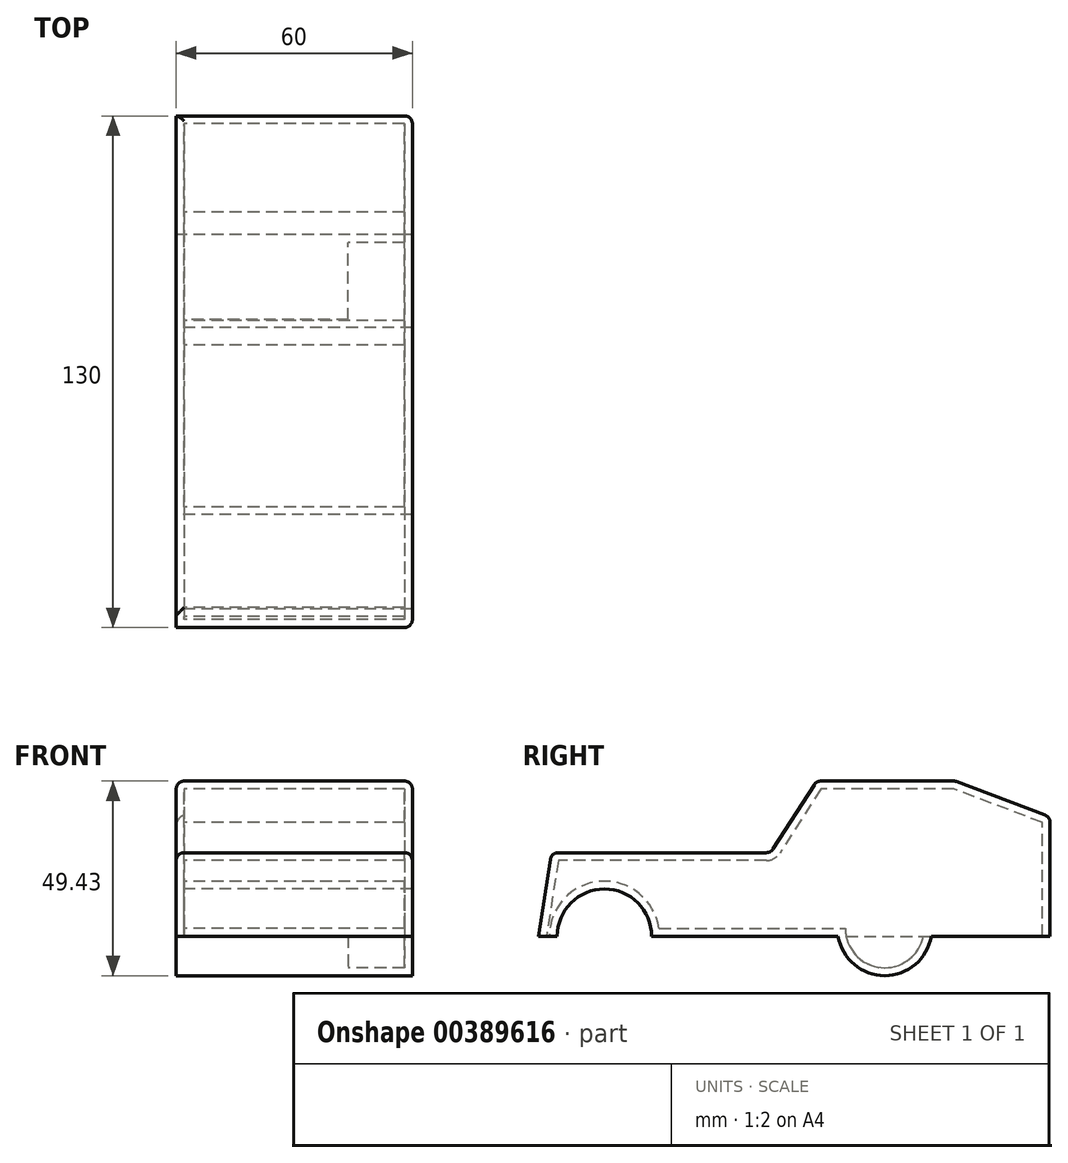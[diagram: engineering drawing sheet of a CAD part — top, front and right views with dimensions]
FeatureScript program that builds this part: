
annotation { "Feature Type Name" : "Feature", "Feature Type Description" : "" }
export const myFeature = defineFeature(function(context is Context, id is Id, definition is map)
    precondition{}
    {
        {
            var Q0;
            Q0=qCreatedBy(makeId("Right.planeOp"),FACE);
            var sketch = newSketch(context, id + "F0", { "sketchPlane" : qUnion([Q0])});
            skLineSegment(sketch, "E0", {"start": v(-47.15, 0) * mm, "end": v(82.85, 0) * mm});
            skLineSegment(sketch, "E1", {"start": v(82.85, 0) * mm, "end": v(82.85, 30.3) * mm});
            skLineSegment(sketch, "E2", {"start": v(82.85, 30.3) * mm, "end": v(58.75, 39.43) * mm});
            skLineSegment(sketch, "E3", {"start": v(58.75, 39.43) * mm, "end": v(23.55, 39.43) * mm});
            skLineSegment(sketch, "E4", {"start": v(23.55, 39.43) * mm, "end": v(11.9, 21.24) * mm});
            skLineSegment(sketch, "E5", {"start": v(11.9, 21.24) * mm, "end": v(-43.78, 21.24) * mm});
            skLineSegment(sketch, "E6", {"start": v(-43.78, 21.24) * mm, "end": v(-47.15, 0) * mm});
            skCircle(sketch, "E7", {"center": v(-30.37, 0) * mm, "radius": 12 * mm});
            skCircle(sketch, "E8", {"center": v(40.85, 2) * mm, "radius": 12 * mm});
            skSolve(sketch);
        }
        {
            var Q0;
            {var subQ0=sQuery(id+"F0.wireOp",EDGE,"E7");var subQ1=sQuery(id+"F0.wireOp",EDGE,"E0");var subQ2=makeQuery(id+"F0.imprint","INTERSECT",VERTEX,{"disambiguationData":[OD(0.0)],"derivedFrom":[subQ1,subQ0]});Q0=makeQuery(id+"F0.imprint","IMPRINT",FACE,{"disambiguationData":[TD([[makeQuery(id+"F0.imprint","IMPRINT",EDGE,{"disambiguationData":[TD([[subQ2,-1.0]])],"derivedFrom":subQ1}),-1.0]])]});}
            var Q1;
            {var subQ5=sQuery(id+"F0.wireOp",EDGE,"E1");Q1=makeQuery(id+"F0.imprint","IMPRINT",FACE,{"disambiguationData":[TD([[makeQuery(id+"F0.imprint","IMPRINT",EDGE,{"derivedFrom":subQ5}),1.0]])]});}
            var Q2;
            {var subQ0=sQuery(id+"F0.wireOp",EDGE,"E7");var subQ1=sQuery(id+"F0.wireOp",EDGE,"E0");var subQ2=makeQuery(id+"F0.imprint","INTERSECT",VERTEX,{"disambiguationData":[OD(0.0)],"derivedFrom":[subQ1,subQ0]});Q2=makeQuery(id+"F0.imprint","IMPRINT",FACE,{"disambiguationData":[TD([[makeQuery(id+"F0.imprint","IMPRINT",EDGE,{"disambiguationData":[TD([[subQ2,-1.0]])],"derivedFrom":subQ1}),1.0]])]});}
            var Q3;
            {var subQ0=sQuery(id+"F0.wireOp",EDGE,"E8");var subQ1=sQuery(id+"F0.wireOp",EDGE,"E0");var subQ2=makeQuery(id+"F0.imprint","INTERSECT",VERTEX,{"disambiguationData":[OD(0.0)],"derivedFrom":[subQ1,subQ0]});Q3=makeQuery(id+"F0.imprint","IMPRINT",FACE,{"disambiguationData":[TD([[makeQuery(id+"F0.imprint","IMPRINT",EDGE,{"disambiguationData":[TD([[subQ2,-1.0]])],"derivedFrom":subQ1}),1.0]])]});}
            var Q4;
            {var subQ0=sQuery(id+"F0.wireOp",EDGE,"E8");var subQ1=sQuery(id+"F0.wireOp",EDGE,"E0");var subQ2=makeQuery(id+"F0.imprint","INTERSECT",VERTEX,{"disambiguationData":[OD(0.0)],"derivedFrom":[subQ1,subQ0]});Q4=makeQuery(id+"F0.imprint","IMPRINT",FACE,{"disambiguationData":[TD([[makeQuery(id+"F0.imprint","IMPRINT",EDGE,{"disambiguationData":[TD([[subQ2,-1.0]])],"derivedFrom":subQ1}),-1.0]])]});}
            extrude(context, id + "F1", {"entities" : qUnion([Q0, Q1, Q2, Q3, Q4]), "depth" : 60 * mm});
        }
        {
            var Q0;
            Q0=makeQuery(id+"F1.opExtrude","SWEPT_EDGE",EDGE,{"disambiguationData":[OSD([sQuery(id+"F0.wireOp",EDGE,"E5"),sQuery(id+"F0.wireOp",EDGE,"E6")])]});
            var Q1;
            Q1=makeQuery(id+"F1.opExtrude","CAP_EDGE",EDGE,{"disambiguationData":[OSD([sQuery(id+"F0.wireOp",EDGE,"E5")])],"isStart":false});
            var Q2;
            Q2=makeQuery(id+"F1.opExtrude","CAP_EDGE",EDGE,{"disambiguationData":[OSD([sQuery(id+"F0.wireOp",EDGE,"E6")])],"isStart":false});
            var Q3;
            Q3=makeQuery(id+"F1.opExtrude","SWEPT_FACE",FACE,{"disambiguationData":[OSD([sQuery(id+"F0.wireOp",EDGE,"E4")])]});
            var Q4;
            Q4=makeQuery(id+"F1.opExtrude","CAP_EDGE",EDGE,{"disambiguationData":[OSD([sQuery(id+"F0.wireOp",EDGE,"E3")])],"isStart":false});
            var Q5;
            Q5=makeQuery(id+"F1.opExtrude","SWEPT_EDGE",EDGE,{"disambiguationData":[OSD([sQuery(id+"F0.wireOp",EDGE,"E2"),sQuery(id+"F0.wireOp",EDGE,"E3")])]});
            var Q6;
            Q6=makeQuery(id+"F1.opExtrude","CAP_EDGE",EDGE,{"disambiguationData":[OSD([sQuery(id+"F0.wireOp",EDGE,"E2")])],"isStart":false});
            var Q7;
            Q7=makeQuery(id+"F1.opExtrude","SWEPT_EDGE",EDGE,{"disambiguationData":[OSD([sQuery(id+"F0.wireOp",EDGE,"E1"),sQuery(id+"F0.wireOp",EDGE,"E2")])]});
            var Q8;
            Q8=makeQuery(id+"F1.opExtrude","CAP_EDGE",EDGE,{"disambiguationData":[OSD([sQuery(id+"F0.wireOp",EDGE,"E2")])],"isStart":true});
            var Q9;
            Q9=makeQuery(id+"F1.opExtrude","CAP_EDGE",EDGE,{"disambiguationData":[OSD([sQuery(id+"F0.wireOp",EDGE,"E3")])],"isStart":true});
            var Q10;
            Q10=makeQuery(id+"F1.opExtrude","SWEPT_FACE",FACE,{"disambiguationData":[OSD([sQuery(id+"F0.wireOp",EDGE,"E5")])]});
            var Q11;
            Q11=makeQuery(id+"F1.opExtrude","CAP_EDGE",EDGE,{"disambiguationData":[OSD([sQuery(id+"F0.wireOp",EDGE,"E1")])],"isStart":false});
            fillet(context, id + "F2", {"entities" : qUnion([Q0, Q1, Q2, Q3, Q4, Q5, Q6, Q7, Q8, Q9, Q10, Q11]), "radius" : 2 * mm, "tangentPropagation" : true, "allowEdgeOverflow" : false});
        }
        {
            var Q0;
            {var subQ0=sQuery(id+"F0.wireOp",EDGE,"E0");Q0=makeQuery(id+"F1.opExtrude","SWEPT_FACE",FACE,{"disambiguationData":[OSD([subQ0]),TDD([makeQuery(id+"F0.imprint","IMPRINT",EDGE,{"disambiguationData":[TD([[makeQuery(id+"F0.imprint","INTERSECT",VERTEX,{"disambiguationData":[OD(1.0)],"derivedFrom":[subQ0,sQuery(id+"F0.wireOp",EDGE,"E7")]}),-1.0]])],"derivedFrom":subQ0})])]});}
            var Q1;
            {var subQ0=sQuery(id+"F0.wireOp",EDGE,"E0");Q1=makeQuery(id+"F1.opExtrude","SWEPT_FACE",FACE,{"disambiguationData":[OSD([subQ0]),TDD([makeQuery(id+"F0.imprint","IMPRINT",EDGE,{"disambiguationData":[TD([[makeQuery(id+"F0.imprint","INTERSECT",VERTEX,{"derivedFrom":[subQ0,sQuery(id+"F0.wireOp",EDGE,"E1")]}),1.0]])],"derivedFrom":subQ0})])]});}
            var Q2;
            {var subQ0=sQuery(id+"F0.wireOp",EDGE,"E0");Q2=makeQuery(id+"F1.opExtrude","SWEPT_FACE",FACE,{"disambiguationData":[OSD([subQ0]),TDD([makeQuery(id+"F0.imprint","IMPRINT",EDGE,{"disambiguationData":[TD([[makeQuery(id+"F0.imprint","INTERSECT",VERTEX,{"derivedFrom":[subQ0,sQuery(id+"F0.wireOp",EDGE,"E6")]}),-1.0]])],"derivedFrom":subQ0})])]});}
            shell(context, id + "F3", {"entities" : qUnion([Q0, Q1, Q2]), "thickness" : 2 * mm});
        }
        {
            var Q0;
            {var subQ0=sQuery(id+"F0.wireOp",EDGE,"E8");var subQ1=sQuery(id+"F0.wireOp",EDGE,"E0");var subQ2=makeQuery(id+"F0.imprint","INTERSECT",VERTEX,{"disambiguationData":[OD(0.0)],"derivedFrom":[subQ1,subQ0]});Q0=makeQuery(id+"F0.imprint","IMPRINT",FACE,{"disambiguationData":[TD([[makeQuery(id+"F0.imprint","IMPRINT",EDGE,{"disambiguationData":[TD([[subQ2,-1.0]])],"derivedFrom":subQ1}),-1.0]])]});}
            var Q1;
            {var subQ0=sQuery(id+"F0.wireOp",EDGE,"E7");var subQ1=sQuery(id+"F0.wireOp",EDGE,"E0");var subQ2=makeQuery(id+"F0.imprint","INTERSECT",VERTEX,{"disambiguationData":[OD(0.0)],"derivedFrom":[subQ1,subQ0]});Q1=makeQuery(id+"F0.imprint","IMPRINT",FACE,{"disambiguationData":[TD([[makeQuery(id+"F0.imprint","IMPRINT",EDGE,{"disambiguationData":[TD([[subQ2,-1.0]])],"derivedFrom":subQ1}),-1.0]])]});}
            extrude(context, id + "F4", {"entities" : qUnion([Q0, Q1]), "operationType" : NewBodyOperationType.ADD, "depth" : 43.7 * mm});
        }
        {
            var Q0;
            Q0=sQuery(id+"F0.wireOp",EDGE,"E8");
            var Q1;
            Q1=sQuery(id+"F0.wireOp",EDGE,"E7");
            extrude(context, id + "F5", {"bodyType" : ToolBodyType.SURFACE, "surfaceEntities" : qUnion([Q0, Q1]), "oppositeDirection" : true, "depth" : 8 * mm, "hasSecondDirection" : true, "secondDirectionOppositeDirection" : false, "secondDirectionDepth" : 68.8 * mm});
        }
    });
